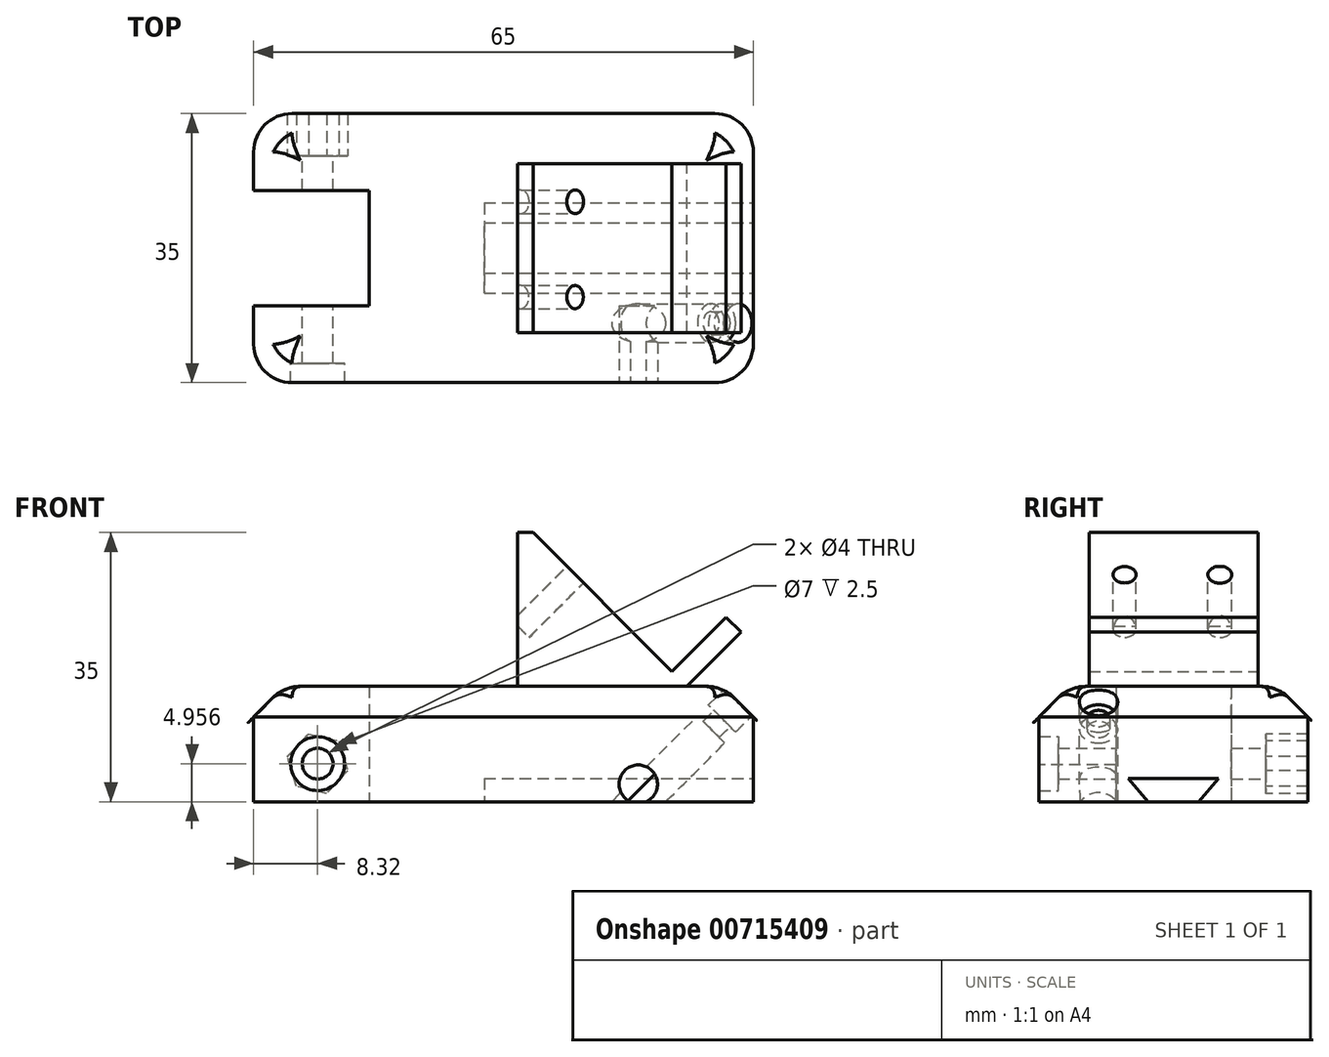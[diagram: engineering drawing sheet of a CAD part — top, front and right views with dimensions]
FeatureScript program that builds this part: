
annotation { "Feature Type Name" : "Feature", "Feature Type Description" : "" }
export const myFeature = defineFeature(function(context is Context, id is Id, definition is map)
    precondition{}
    {
        {
            var Q0;
            Q0=qCreatedBy(makeId("Top.planeOp"),FACE);
            var sketch = newSketch(context, id + "F0", { "sketchPlane" : qUnion([Q0])});
            skLineSegment(sketch, "E0.bottom", {"start": v(27.5, -17.5) * mm, "end": v(-27.5, -17.5) * mm});
            skLineSegment(sketch, "E0.top", {"start": v(27.5, 17.5) * mm, "end": v(-27.5, 17.5) * mm});
            skLineSegment(sketch, "E0.left", {"start": v(32.5, -12.5) * mm, "end": v(32.5, 12.5) * mm});
            skLineSegment(sketch, "E0.right", {"start": v(-32.5, -12.5) * mm, "end": v(-32.5, 12.5) * mm});
            skPoint(sketch, "E0.middle", {"position": v(0, 0) * mm});
            skPoint(sketch, "E1.visualSharp", {"position": v(-32.5, 17.5) * mm});
            skArc(sketch, "E1.filletArc", {"start": v(-27.5, 17.5) * mm, "mid": v(-31.04, 16.04) * mm, "end": v(-32.5, 12.5) * mm});
            skPoint(sketch, "E2.visualSharp", {"position": v(32.5, 17.5) * mm});
            skArc(sketch, "E2.filletArc", {"start": v(32.5, 12.5) * mm, "mid": v(31.04, 16.04) * mm, "end": v(27.5, 17.5) * mm});
            skPoint(sketch, "E3.visualSharp", {"position": v(32.5, -17.5) * mm});
            skArc(sketch, "E3.filletArc", {"start": v(27.5, -17.5) * mm, "mid": v(31.04, -16.04) * mm, "end": v(32.5, -12.5) * mm});
            skPoint(sketch, "E4.visualSharp", {"position": v(-32.5, -17.5) * mm});
            skArc(sketch, "E4.filletArc", {"start": v(-32.5, -12.5) * mm, "mid": v(-31.04, -16.04) * mm, "end": v(-27.5, -17.5) * mm});
            skLineSegment(sketch, "E5.bottom", {"start": v(-17.5, -7.5) * mm, "end": v(-32.5, -7.5) * mm});
            skLineSegment(sketch, "E5.top", {"start": v(-17.5, 7.5) * mm, "end": v(-32.5, 7.5) * mm});
            skLineSegment(sketch, "E5.left", {"start": v(-17.5, -7.5) * mm, "end": v(-17.5, 7.5) * mm});
            skLineSegment(sketch, "E5.right", {"start": v(-32.5, -7.5) * mm, "end": v(-32.5, 7.5) * mm});
            skPoint(sketch, "E5.middle", {"position": v(-25, 0) * mm});
            skSolve(sketch);
        }
        {
            var Q0;
            Q0=makeQuery(id+"F0.imprint","IMPRINT",FACE,{"disambiguationData":[TD([[makeQuery(id+"F0.imprint","IMPRINT",EDGE,{"derivedFrom":sQuery(id+"F0.wireOp",EDGE,"E0.bottom")}),-1.0]])]});
            extrude(context, id + "F1", {"entities" : qUnion([Q0]), "depth" : 15 * mm, "offsetDistance" : 25 * mm});
        }
        {
            var Q0;
            Q0=qCreatedBy(makeId("Front.planeOp"),FACE);
            var sketch = newSketch(context, id + "F2", { "sketchPlane" : qUnion([Q0])});
            skCircle(sketch, "E6", {"center": v(-24.18, 4.96) * mm, "radius": 2 * mm});
            skCircle(sketch, "E7.0", {"center": v(-24.18, 4.96) * mm, "radius": 3.5 * mm});
            skCircle(sketch, "E8.cCircle", {"center": v(-24.18, 4.96) * mm, "radius": 3.5 * mm, "construction": true});
            skLineSegment(sketch, "E8.0", {"start": v(-20.25, 4.03) * mm, "end": v(-23.02, 1.08) * mm});
            skLineSegment(sketch, "E8.1", {"start": v(-23.02, 1.08) * mm, "end": v(-26.95, 2.01) * mm});
            skLineSegment(sketch, "E8.2", {"start": v(-26.95, 2.01) * mm, "end": v(-28.11, 5.89) * mm});
            skLineSegment(sketch, "E8.3", {"start": v(-28.11, 5.89) * mm, "end": v(-25.34, 8.83) * mm});
            skLineSegment(sketch, "E8.4", {"start": v(-25.34, 8.83) * mm, "end": v(-21.4, 7.9) * mm});
            skLineSegment(sketch, "E8.5", {"start": v(-21.4, 7.9) * mm, "end": v(-20.25, 4.03) * mm});
            skPoint(sketch, "E8.0.midPoint", {"position": v(-21.63, 2.56) * mm});
            skSolve(sketch);
        }
        {
            var Q0;
            Q0=makeQuery(id+"F2.imprint","IMPRINT",FACE,{"disambiguationData":[TD([[makeQuery(id+"F2.imprint","IMPRINT",EDGE,{"derivedFrom":sQuery(id+"F2.wireOp",EDGE,"E6")}),-1.0]])]});
            var Q1;
            {var subQ0=sQuery(id+"F2.wireOp",EDGE,"E8.2");var subQ1=sQuery(id+"F2.wireOp",EDGE,"E7.0");var subQ2=makeQuery(id+"F2.imprint","INTERSECT",VERTEX,{"derivedFrom":[subQ1,subQ0]});Q1=makeQuery(id+"F2.imprint","IMPRINT",FACE,{"disambiguationData":[TD([[makeQuery(id+"F2.imprint","IMPRINT",EDGE,{"disambiguationData":[TD([[subQ2,-1.0]])],"derivedFrom":subQ1}),-1.0]])]});}
            var Q2;
            {var subQ0=sQuery(id+"F2.wireOp",EDGE,"E8.3");var subQ1=sQuery(id+"F2.wireOp",EDGE,"E7.0");var subQ2=makeQuery(id+"F2.imprint","INTERSECT",VERTEX,{"derivedFrom":[subQ1,subQ0]});Q2=makeQuery(id+"F2.imprint","IMPRINT",FACE,{"disambiguationData":[TD([[makeQuery(id+"F2.imprint","IMPRINT",EDGE,{"disambiguationData":[TD([[subQ2,-1.0]])],"derivedFrom":subQ1}),-1.0]])]});}
            var Q3;
            {var subQ0=sQuery(id+"F2.wireOp",EDGE,"E8.4");var subQ1=sQuery(id+"F2.wireOp",EDGE,"E7.0");var subQ2=makeQuery(id+"F2.imprint","INTERSECT",VERTEX,{"derivedFrom":[subQ1,subQ0]});Q3=makeQuery(id+"F2.imprint","IMPRINT",FACE,{"disambiguationData":[TD([[makeQuery(id+"F2.imprint","IMPRINT",EDGE,{"disambiguationData":[TD([[subQ2,-1.0]])],"derivedFrom":subQ1}),-1.0]])]});}
            var Q4;
            {var subQ0=sQuery(id+"F2.wireOp",EDGE,"E8.4");var subQ1=sQuery(id+"F2.wireOp",EDGE,"E7.0");var subQ2=makeQuery(id+"F2.imprint","INTERSECT",VERTEX,{"derivedFrom":[subQ1,subQ0]});Q4=makeQuery(id+"F2.imprint","IMPRINT",FACE,{"disambiguationData":[TD([[makeQuery(id+"F2.imprint","IMPRINT",EDGE,{"disambiguationData":[TD([[subQ2,1.0]])],"derivedFrom":subQ1}),-1.0]])]});}
            var Q5;
            {var subQ0=sQuery(id+"F2.wireOp",EDGE,"E8.5");var subQ1=sQuery(id+"F2.wireOp",EDGE,"E7.0");var subQ2=makeQuery(id+"F2.imprint","INTERSECT",VERTEX,{"derivedFrom":[subQ1,subQ0]});Q5=makeQuery(id+"F2.imprint","IMPRINT",FACE,{"disambiguationData":[TD([[makeQuery(id+"F2.imprint","IMPRINT",EDGE,{"disambiguationData":[TD([[subQ2,1.0]])],"derivedFrom":subQ1}),-1.0]])]});}
            var Q6;
            {var subQ0=sQuery(id+"F2.wireOp",EDGE,"E8.1");var subQ1=sQuery(id+"F2.wireOp",EDGE,"E7.0");var subQ2=makeQuery(id+"F2.imprint","INTERSECT",VERTEX,{"derivedFrom":[subQ1,subQ0]});Q6=makeQuery(id+"F2.imprint","IMPRINT",FACE,{"disambiguationData":[TD([[makeQuery(id+"F2.imprint","IMPRINT",EDGE,{"disambiguationData":[TD([[subQ2,-1.0]])],"derivedFrom":subQ1}),-1.0]])]});}
            var Q7;
            Q7=makeQuery(id+"F1.opExtrude","SWEPT_BODY",BODY,{"disambiguationData":[OSD([sQuery(id+"F0.wireOp",EDGE,"E0.bottom"),sQuery(id+"F0.wireOp",EDGE,"E0.top"),sQuery(id+"F0.wireOp",EDGE,"E0.left"),sQuery(id+"F0.wireOp",EDGE,"E0.right"),sQuery(id+"F0.wireOp",EDGE,"E1.filletArc"),sQuery(id+"F0.wireOp",EDGE,"E2.filletArc"),sQuery(id+"F0.wireOp",EDGE,"E3.filletArc"),sQuery(id+"F0.wireOp",EDGE,"E4.filletArc"),sQuery(id+"F0.wireOp",EDGE,"E5.bottom"),sQuery(id+"F0.wireOp",EDGE,"E5.top"),sQuery(id+"F0.wireOp",EDGE,"E5.left")])]});
            extrude(context, id + "F3", {"entities" : qUnion([Q0, Q1, Q2, Q3, Q4, Q5, Q6]), "operationType" : NewBodyOperationType.REMOVE, "oppositeDirection" : true, "depth" : 37 * mm, "endBoundEntityBody" : qUnion([Q7]), "hasOffset" : true, "offsetDistance" : 27 * mm, "hasSecondDirection" : true, "secondDirectionOppositeDirection" : true, "secondDirectionDepth" : 12 * mm});
        }
        {
            var Q0;
            Q0=makeQuery(id+"F2.imprint","IMPRINT",FACE,{"disambiguationData":[TD([[makeQuery(id+"F2.imprint","IMPRINT",EDGE,{"derivedFrom":sQuery(id+"F2.wireOp",EDGE,"E6")}),-1.0]])]});
            extrude(context, id + "F4", {"entities" : qUnion([Q0]), "operationType" : NewBodyOperationType.REMOVE, "depth" : 40 * mm, "offsetDistance" : 25 * mm, "hasSecondDirection" : true, "secondDirectionOppositeDirection" : false, "secondDirectionDepth" : 15 * mm});
        }
        {
            var Q0;
            Q0=makeQuery(id+"F2.imprint","IMPRINT",FACE,{"disambiguationData":[TD([[makeQuery(id+"F2.imprint","IMPRINT",EDGE,{"derivedFrom":sQuery(id+"F2.wireOp",EDGE,"E6")}),1.0]])]});
            extrude(context, id + "F5", {"entities" : qUnion([Q0]), "operationType" : NewBodyOperationType.REMOVE, "endBound" : BoundingType.SYMMETRIC, "depth" : 50 * mm, "offsetDistance" : 25 * mm});
        }
        {
            var Q0;
            Q0=makeQuery(id+"F1.opExtrude","CAP_FACE",FACE,{"disambiguationData":[OSD([sQuery(id+"F0.wireOp",EDGE,"E0.bottom"),sQuery(id+"F0.wireOp",EDGE,"E0.top"),sQuery(id+"F0.wireOp",EDGE,"E0.left"),sQuery(id+"F0.wireOp",EDGE,"E0.right"),sQuery(id+"F0.wireOp",EDGE,"E1.filletArc"),sQuery(id+"F0.wireOp",EDGE,"E2.filletArc"),sQuery(id+"F0.wireOp",EDGE,"E3.filletArc"),sQuery(id+"F0.wireOp",EDGE,"E4.filletArc"),sQuery(id+"F0.wireOp",EDGE,"E5.bottom"),sQuery(id+"F0.wireOp",EDGE,"E5.top"),sQuery(id+"F0.wireOp",EDGE,"E5.left")])],"isStart":false});
            var sketch = newSketch(context, id + "F6", { "sketchPlane" : qUnion([Q0])});
            skLineSegment(sketch, "E9.bottom", {"start": v(23.83, -11) * mm, "end": v(1.83, -11) * mm});
            skLineSegment(sketch, "E9.top", {"start": v(23.83, 11) * mm, "end": v(1.83, 11) * mm});
            skLineSegment(sketch, "E9.left", {"start": v(23.83, -11) * mm, "end": v(23.83, 11) * mm});
            skLineSegment(sketch, "E9.right", {"start": v(1.83, -11) * mm, "end": v(1.83, 11) * mm});
            skPoint(sketch, "E9.middle", {"position": v(12.83, 0) * mm});
            skSolve(sketch);
        }
        {
            var Q0;
            Q0=makeQuery(id+"F6.imprint","IMPRINT",FACE,{"disambiguationData":[TD([[makeQuery(id+"F6.imprint","IMPRINT",EDGE,{"derivedFrom":sQuery(id+"F6.wireOp",EDGE,"E9.bottom")}),-1.0]])]});
            extrude(context, id + "F7", {"entities" : qUnion([Q0]), "operationType" : NewBodyOperationType.ADD, "depth" : 20 * mm, "offsetDistance" : 25 * mm});
        }
        {
            var Q0;
            Q0=makeQuery(id+"F7.opExtrude","CAP_EDGE",EDGE,{"disambiguationData":[OSD([sQuery(id+"F6.wireOp",EDGE,"E9.left")])],"isStart":false});
            chamfer(context, id + "F8", {"entities" : qUnion([Q0]), "width" : 20 * mm, "tangentPropagation" : true});
        }
        {
            var Q0;
            Q0=makeQuery(id+"F1.opExtrude","SWEPT_FACE",FACE,{"disambiguationData":[OSD([sQuery(id+"F0.wireOp",EDGE,"E0.left")])]});
            var sketch = newSketch(context, id + "F9", { "sketchPlane" : qUnion([Q0])});
            skLineSegment(sketch, "E10.bottom", {"start": v(5.87, 0) * mm, "end": v(-5.87, 0) * mm});
            skLineSegment(sketch, "E10.top", {"start": v(5.87, 3.04) * mm, "end": v(-5.87, 3.04) * mm});
            skLineSegment(sketch, "E10.left", {"start": v(5.87, 0) * mm, "end": v(5.87, 3.04) * mm});
            skLineSegment(sketch, "E10.right", {"start": v(-5.87, 0) * mm, "end": v(-5.87, 3.04) * mm});
            skPoint(sketch, "E10.middle", {"position": v(0, 1.52) * mm});
            skLineSegment(sketch, "E11", {"start": v(-5.87, 3.04) * mm, "end": v(-3.27, 0) * mm});
            skLineSegment(sketch, "E12", {"start": v(5.87, 3.04) * mm, "end": v(3.27, 0) * mm});
            skSolve(sketch);
        }
        {
            var Q0;
            Q0=makeQuery(id+"F9.imprint","IMPRINT",FACE,{"disambiguationData":[TD([[makeQuery(id+"F9.imprint","IMPRINT",EDGE,{"derivedFrom":sQuery(id+"F9.wireOp",EDGE,"E10.top")}),1.0]])]});
            extrude(context, id + "F10", {"entities" : qUnion([Q0]), "operationType" : NewBodyOperationType.REMOVE, "oppositeDirection" : true, "depth" : 35 * mm, "offsetDistance" : 25 * mm});
        }
        {
            var Q0;
            Q0=makeQuery(id+"F8.opChamfer","BLEND_FACE",FACE,{"disambiguationData":[OSD([sQuery(id+"F6.wireOp",EDGE,"E9.left")])]});
            var sketch = newSketch(context, id + "F11", { "sketchPlane" : qUnion([Q0])});
            skCircle(sketch, "E13", {"center": v(-6.37, 14.29) * mm, "radius": 1.5 * mm});
            skCircle(sketch, "E14", {"center": v(6.02, 14.29) * mm, "radius": 1.55 * mm});
            skSolve(sketch);
        }
        {
            var Q0;
            Q0=makeQuery(id+"F11.imprint","IMPRINT",FACE,{"disambiguationData":[TD([[makeQuery(id+"F11.imprint","IMPRINT",EDGE,{"derivedFrom":sQuery(id+"F11.wireOp",EDGE,"E13")}),1.0]])]});
            var Q1;
            Q1=makeQuery(id+"F11.imprint","IMPRINT",FACE,{"disambiguationData":[TD([[makeQuery(id+"F11.imprint","IMPRINT",EDGE,{"derivedFrom":sQuery(id+"F11.wireOp",EDGE,"E14")}),1.0]])]});
            extrude(context, id + "F12", {"entities" : qUnion([Q0, Q1]), "operationType" : NewBodyOperationType.REMOVE, "oppositeDirection" : true, "depth" : 10 * mm, "offsetDistance" : 25 * mm});
        }
        {
            var Q0;
            Q0=makeQuery(id+"F1.opExtrude","CAP_EDGE",EDGE,{"disambiguationData":[OSD([sQuery(id+"F0.wireOp",EDGE,"E0.left")])],"isStart":false});
            var Q1;
            Q1=makeQuery(id+"F1.opExtrude","CAP_EDGE",EDGE,{"disambiguationData":[OSD([sQuery(id+"F0.wireOp",EDGE,"E3.filletArc")])],"isStart":false});
            var Q2;
            Q2=makeQuery(id+"F1.opExtrude","CAP_EDGE",EDGE,{"disambiguationData":[OSD([sQuery(id+"F0.wireOp",EDGE,"E2.filletArc")])],"isStart":false});
            chamfer(context, id + "F13", {"entities" : qUnion([Q0, Q1, Q2]), "width" : 4 * mm, "tangentPropagation" : true});
        }
        {
            var Q0;
            Q0=makeQuery(id+"F13.opChamfer","BLEND_FACE",FACE,{"disambiguationData":[OSD([sQuery(id+"F0.wireOp",EDGE,"E0.left")])]});
            var sketch = newSketch(context, id + "F14", { "sketchPlane" : qUnion([Q0])});
            skCircle(sketch, "E15", {"center": v(-9.75, -12.44) * mm, "radius": 2.5 * mm});
            skCircle(sketch, "E16.0", {"center": v(-9.75, -12.44) * mm, "radius": 1.5 * mm});
            skSolve(sketch);
        }
        {
            var Q0;
            Q0=makeQuery(id+"F14.imprint","IMPRINT",FACE,{"disambiguationData":[TD([[makeQuery(id+"F14.imprint","IMPRINT",EDGE,{"derivedFrom":sQuery(id+"F14.wireOp",EDGE,"E15")}),1.0]])]});
            var Q1;
            Q1=makeQuery(id+"F14.imprint","IMPRINT",FACE,{"disambiguationData":[TD([[makeQuery(id+"F14.imprint","IMPRINT",EDGE,{"derivedFrom":sQuery(id+"F14.wireOp",EDGE,"E16.0")}),1.0]])]});
            extrude(context, id + "F15", {"entities" : qUnion([Q0, Q1]), "operationType" : NewBodyOperationType.REMOVE, "oppositeDirection" : true, "depth" : 22 * mm, "offsetDistance" : 25 * mm});
        }
        {
            var Q0;
            Q0=makeQuery(id+"F14.imprint","IMPRINT",FACE,{"disambiguationData":[TD([[makeQuery(id+"F14.imprint","IMPRINT",EDGE,{"derivedFrom":sQuery(id+"F14.wireOp",EDGE,"E15")}),1.0]])]});
            extrude(context, id + "F16", {"entities" : qUnion([Q0]), "operationType" : NewBodyOperationType.ADD, "oppositeDirection" : true, "depth" : 5 * mm, "offsetDistance" : 25 * mm, "hasSecondDirection" : true, "secondDirectionOppositeDirection" : true, "secondDirectionDepth" : 3 * mm});
        }
        {
            var Q0;
            Q0=makeQuery(id+"F8.opChamfer","BLEND_FACE",FACE,{"disambiguationData":[OSD([sQuery(id+"F6.wireOp",EDGE,"E9.left")])]});
            var sketch = newSketch(context, id + "F17", { "sketchPlane" : qUnion([Q0])});
            skLineSegment(sketch, "E17.bottom", {"start": v(-11, -3.5) * mm, "end": v(11, -3.5) * mm});
            skLineSegment(sketch, "E17.top", {"start": v(-11, -6.25) * mm, "end": v(11, -6.25) * mm});
            skLineSegment(sketch, "E17.left", {"start": v(-11, -3.5) * mm, "end": v(-11, -6.25) * mm});
            skLineSegment(sketch, "E17.right", {"start": v(11, -3.5) * mm, "end": v(11, -6.25) * mm});
            skSolve(sketch);
        }
        {
            var Q0;
            Q0 = qSketchRegion(id + "F17", true);
            extrude(context, id + "F18", {"entities" : qUnion([Q0]), "operationType" : NewBodyOperationType.ADD, "depth" : 10 * mm, "offsetDistance" : 25 * mm});
        }
        {
            var Q0;
            {var subQ0=sQuery(id+"F0.wireOp",EDGE,"E0.bottom");Q0=makeQuery(id+"F13.opChamfer","BLEND_EDGE",EDGE,{"blendedFrom":[makeQuery(id+"F1.opExtrude","CAP_EDGE",EDGE,{"disambiguationData":[OSD([subQ0])],"isStart":false}),makeQuery(id+"F1.opExtrude","CAP_FACE",FACE,{"disambiguationData":[OSD([subQ0,sQuery(id+"F0.wireOp",EDGE,"E0.top"),sQuery(id+"F0.wireOp",EDGE,"E0.left"),sQuery(id+"F0.wireOp",EDGE,"E0.right"),sQuery(id+"F0.wireOp",EDGE,"E1.filletArc"),sQuery(id+"F0.wireOp",EDGE,"E2.filletArc"),sQuery(id+"F0.wireOp",EDGE,"E3.filletArc"),sQuery(id+"F0.wireOp",EDGE,"E4.filletArc"),sQuery(id+"F0.wireOp",EDGE,"E5.bottom"),sQuery(id+"F0.wireOp",EDGE,"E5.top"),sQuery(id+"F0.wireOp",EDGE,"E5.left")])],"isStart":false})],"blendedInto":[makeQuery(id+"F1.opExtrude","CAP_FACE",FACE,{"disambiguationData":[OSD([subQ0,sQuery(id+"F0.wireOp",EDGE,"E0.top"),sQuery(id+"F0.wireOp",EDGE,"E0.left"),sQuery(id+"F0.wireOp",EDGE,"E0.right"),sQuery(id+"F0.wireOp",EDGE,"E1.filletArc"),sQuery(id+"F0.wireOp",EDGE,"E2.filletArc"),sQuery(id+"F0.wireOp",EDGE,"E3.filletArc"),sQuery(id+"F0.wireOp",EDGE,"E4.filletArc"),sQuery(id+"F0.wireOp",EDGE,"E5.bottom"),sQuery(id+"F0.wireOp",EDGE,"E5.top"),sQuery(id+"F0.wireOp",EDGE,"E5.left")])],"isStart":false})]});}
            var Q1;
            {var subQ0=sQuery(id+"F0.wireOp",EDGE,"E4.filletArc");Q1=makeQuery(id+"F13.opChamfer","BLEND_EDGE",EDGE,{"blendedFrom":[makeQuery(id+"F1.opExtrude","CAP_EDGE",EDGE,{"disambiguationData":[OSD([subQ0])],"isStart":false}),makeQuery(id+"F1.opExtrude","CAP_FACE",FACE,{"disambiguationData":[OSD([sQuery(id+"F0.wireOp",EDGE,"E0.bottom"),sQuery(id+"F0.wireOp",EDGE,"E0.top"),sQuery(id+"F0.wireOp",EDGE,"E0.left"),sQuery(id+"F0.wireOp",EDGE,"E0.right"),sQuery(id+"F0.wireOp",EDGE,"E1.filletArc"),sQuery(id+"F0.wireOp",EDGE,"E2.filletArc"),sQuery(id+"F0.wireOp",EDGE,"E3.filletArc"),subQ0,sQuery(id+"F0.wireOp",EDGE,"E5.bottom"),sQuery(id+"F0.wireOp",EDGE,"E5.top"),sQuery(id+"F0.wireOp",EDGE,"E5.left")])],"isStart":false})],"blendedInto":[makeQuery(id+"F1.opExtrude","CAP_FACE",FACE,{"disambiguationData":[OSD([sQuery(id+"F0.wireOp",EDGE,"E0.bottom"),sQuery(id+"F0.wireOp",EDGE,"E0.top"),sQuery(id+"F0.wireOp",EDGE,"E0.left"),sQuery(id+"F0.wireOp",EDGE,"E0.right"),sQuery(id+"F0.wireOp",EDGE,"E1.filletArc"),sQuery(id+"F0.wireOp",EDGE,"E2.filletArc"),sQuery(id+"F0.wireOp",EDGE,"E3.filletArc"),subQ0,sQuery(id+"F0.wireOp",EDGE,"E5.bottom"),sQuery(id+"F0.wireOp",EDGE,"E5.top"),sQuery(id+"F0.wireOp",EDGE,"E5.left")])],"isStart":false})]});}
            var Q2;
            {var subQ0=sQuery(id+"F0.wireOp",EDGE,"E0.top");Q2=makeQuery(id+"F13.opChamfer","BLEND_EDGE",EDGE,{"blendedFrom":[makeQuery(id+"F1.opExtrude","CAP_EDGE",EDGE,{"disambiguationData":[OSD([subQ0])],"isStart":false}),makeQuery(id+"F1.opExtrude","CAP_FACE",FACE,{"disambiguationData":[OSD([sQuery(id+"F0.wireOp",EDGE,"E0.bottom"),subQ0,sQuery(id+"F0.wireOp",EDGE,"E0.left"),sQuery(id+"F0.wireOp",EDGE,"E0.right"),sQuery(id+"F0.wireOp",EDGE,"E1.filletArc"),sQuery(id+"F0.wireOp",EDGE,"E2.filletArc"),sQuery(id+"F0.wireOp",EDGE,"E3.filletArc"),sQuery(id+"F0.wireOp",EDGE,"E4.filletArc"),sQuery(id+"F0.wireOp",EDGE,"E5.bottom"),sQuery(id+"F0.wireOp",EDGE,"E5.top"),sQuery(id+"F0.wireOp",EDGE,"E5.left")])],"isStart":false})],"blendedInto":[makeQuery(id+"F1.opExtrude","CAP_FACE",FACE,{"disambiguationData":[OSD([sQuery(id+"F0.wireOp",EDGE,"E0.bottom"),subQ0,sQuery(id+"F0.wireOp",EDGE,"E0.left"),sQuery(id+"F0.wireOp",EDGE,"E0.right"),sQuery(id+"F0.wireOp",EDGE,"E1.filletArc"),sQuery(id+"F0.wireOp",EDGE,"E2.filletArc"),sQuery(id+"F0.wireOp",EDGE,"E3.filletArc"),sQuery(id+"F0.wireOp",EDGE,"E4.filletArc"),sQuery(id+"F0.wireOp",EDGE,"E5.bottom"),sQuery(id+"F0.wireOp",EDGE,"E5.top"),sQuery(id+"F0.wireOp",EDGE,"E5.left")])],"isStart":false})]});}
            var Q3;
            {var subQ0=sQuery(id+"F0.wireOp",EDGE,"E1.filletArc");Q3=makeQuery(id+"F13.opChamfer","BLEND_EDGE",EDGE,{"blendedFrom":[makeQuery(id+"F1.opExtrude","CAP_EDGE",EDGE,{"disambiguationData":[OSD([subQ0])],"isStart":false}),makeQuery(id+"F1.opExtrude","CAP_FACE",FACE,{"disambiguationData":[OSD([sQuery(id+"F0.wireOp",EDGE,"E0.bottom"),sQuery(id+"F0.wireOp",EDGE,"E0.top"),sQuery(id+"F0.wireOp",EDGE,"E0.left"),sQuery(id+"F0.wireOp",EDGE,"E0.right"),subQ0,sQuery(id+"F0.wireOp",EDGE,"E2.filletArc"),sQuery(id+"F0.wireOp",EDGE,"E3.filletArc"),sQuery(id+"F0.wireOp",EDGE,"E4.filletArc"),sQuery(id+"F0.wireOp",EDGE,"E5.bottom"),sQuery(id+"F0.wireOp",EDGE,"E5.top"),sQuery(id+"F0.wireOp",EDGE,"E5.left")])],"isStart":false})],"blendedInto":[makeQuery(id+"F1.opExtrude","CAP_FACE",FACE,{"disambiguationData":[OSD([sQuery(id+"F0.wireOp",EDGE,"E0.bottom"),sQuery(id+"F0.wireOp",EDGE,"E0.top"),sQuery(id+"F0.wireOp",EDGE,"E0.left"),sQuery(id+"F0.wireOp",EDGE,"E0.right"),subQ0,sQuery(id+"F0.wireOp",EDGE,"E2.filletArc"),sQuery(id+"F0.wireOp",EDGE,"E3.filletArc"),sQuery(id+"F0.wireOp",EDGE,"E4.filletArc"),sQuery(id+"F0.wireOp",EDGE,"E5.bottom"),sQuery(id+"F0.wireOp",EDGE,"E5.top"),sQuery(id+"F0.wireOp",EDGE,"E5.left")])],"isStart":false})]});}
            fillet(context, id + "F19", {"entities" : qUnion([Q0, Q1, Q2, Q3]), "radius" : 5 * mm, "tangentPropagation" : true, "allowEdgeOverflow" : false});
        }
        {
            var Q0;
            {var subQ1=sQuery(id+"F0.wireOp",EDGE,"E3.filletArc");var subQ10=sQuery(id+"F0.wireOp",EDGE,"E0.bottom");Q0=makeQuery(id+"F4.boolean.opBoolean","SPLIT",FACE,{"disambiguationData":[TD([makeQuery(id+"F1.opExtrude","SWEPT_FACE",FACE,{"disambiguationData":[OSD([subQ1])]})])],"derivedFrom":makeQuery(id+"F1.opExtrude","SWEPT_FACE",FACE,{"disambiguationData":[OSD([subQ10])]})});}
            var sketch = newSketch(context, id + "F20", { "sketchPlane" : qUnion([Q0])});
            skCircle(sketch, "E18", {"center": v(17.53, 2.28) * mm, "radius": 2.5 * mm});
            skSolve(sketch);
        }
        {
            var Q0;
            Q0 = qSketchRegion(id + "F20", true);
            extrude(context, id + "F21", {"entities" : qUnion([Q0]), "operationType" : NewBodyOperationType.REMOVE, "oppositeDirection" : true, "depth" : 10 * mm, "offsetDistance" : 25 * mm});
        }
    });
